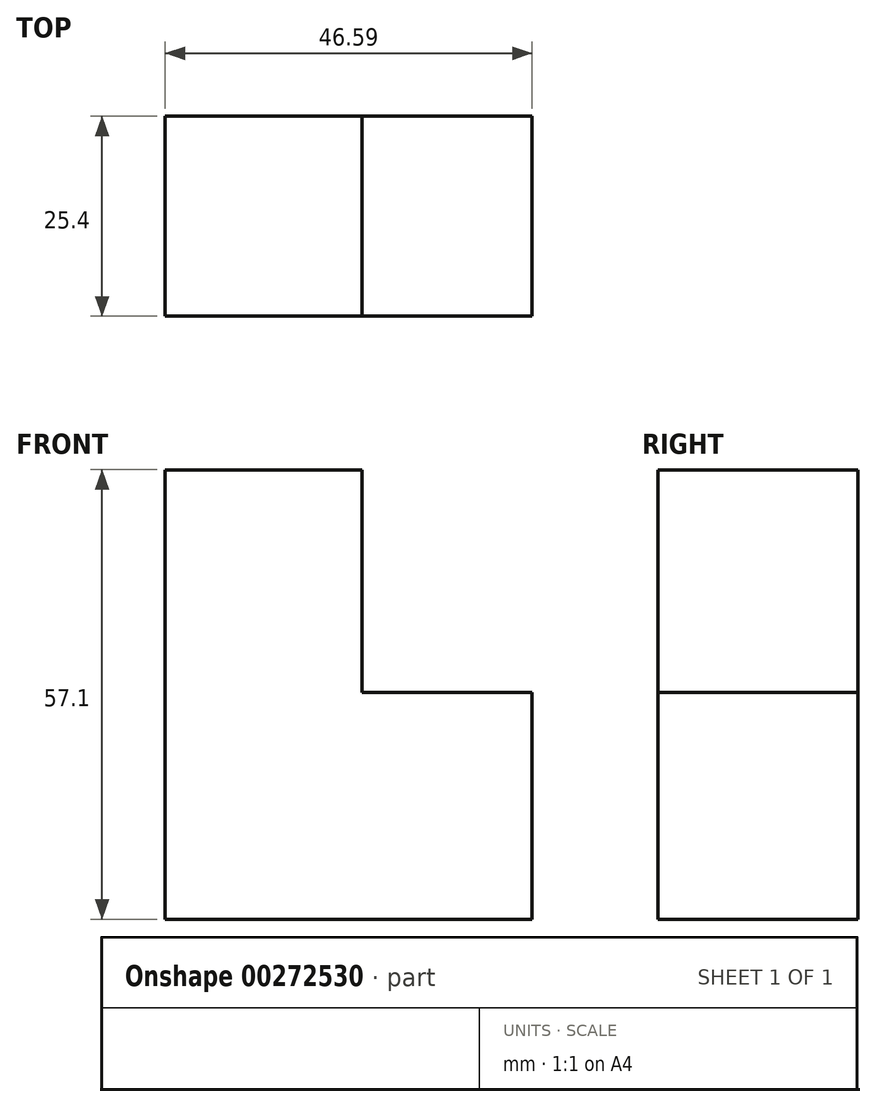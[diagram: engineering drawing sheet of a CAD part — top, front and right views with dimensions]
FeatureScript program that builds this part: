
annotation { "Feature Type Name" : "Feature", "Feature Type Description" : "" }
export const myFeature = defineFeature(function(context is Context, id is Id, definition is map)
    precondition{}
    {
        {
            var Q0;
            Q0=qCreatedBy(makeId("Front.planeOp"),FACE);
            var sketch = newSketch(context, id + "F0", { "sketchPlane" : qUnion([Q0])});
            skLineSegment(sketch, "E0", {"start": v(0, 0) * mm, "end": v(-46.6, 0) * mm});
            skLineSegment(sketch, "E1", {"start": v(-46.6, 0) * mm, "end": v(-46.6, 57.1) * mm});
            skLineSegment(sketch, "E2", {"start": v(-46.6, 57.1) * mm, "end": v(-21.58, 57.1) * mm});
            skLineSegment(sketch, "E3", {"start": v(-21.58, 57.1) * mm, "end": v(-21.58, 28.83) * mm});
            skLineSegment(sketch, "E4", {"start": v(-21.58, 28.83) * mm, "end": v(0, 28.83) * mm});
            skLineSegment(sketch, "E5", {"start": v(0, 28.83) * mm, "end": v(0, 0) * mm});
            skSolve(sketch);
        }
        {
            var Q0;
            Q0 = qSketchRegion(id + "F0", true);
            extrude(context, id + "F1", {"entities" : qUnion([Q0]), "depth" : 25.4 * mm});
        }
    });
